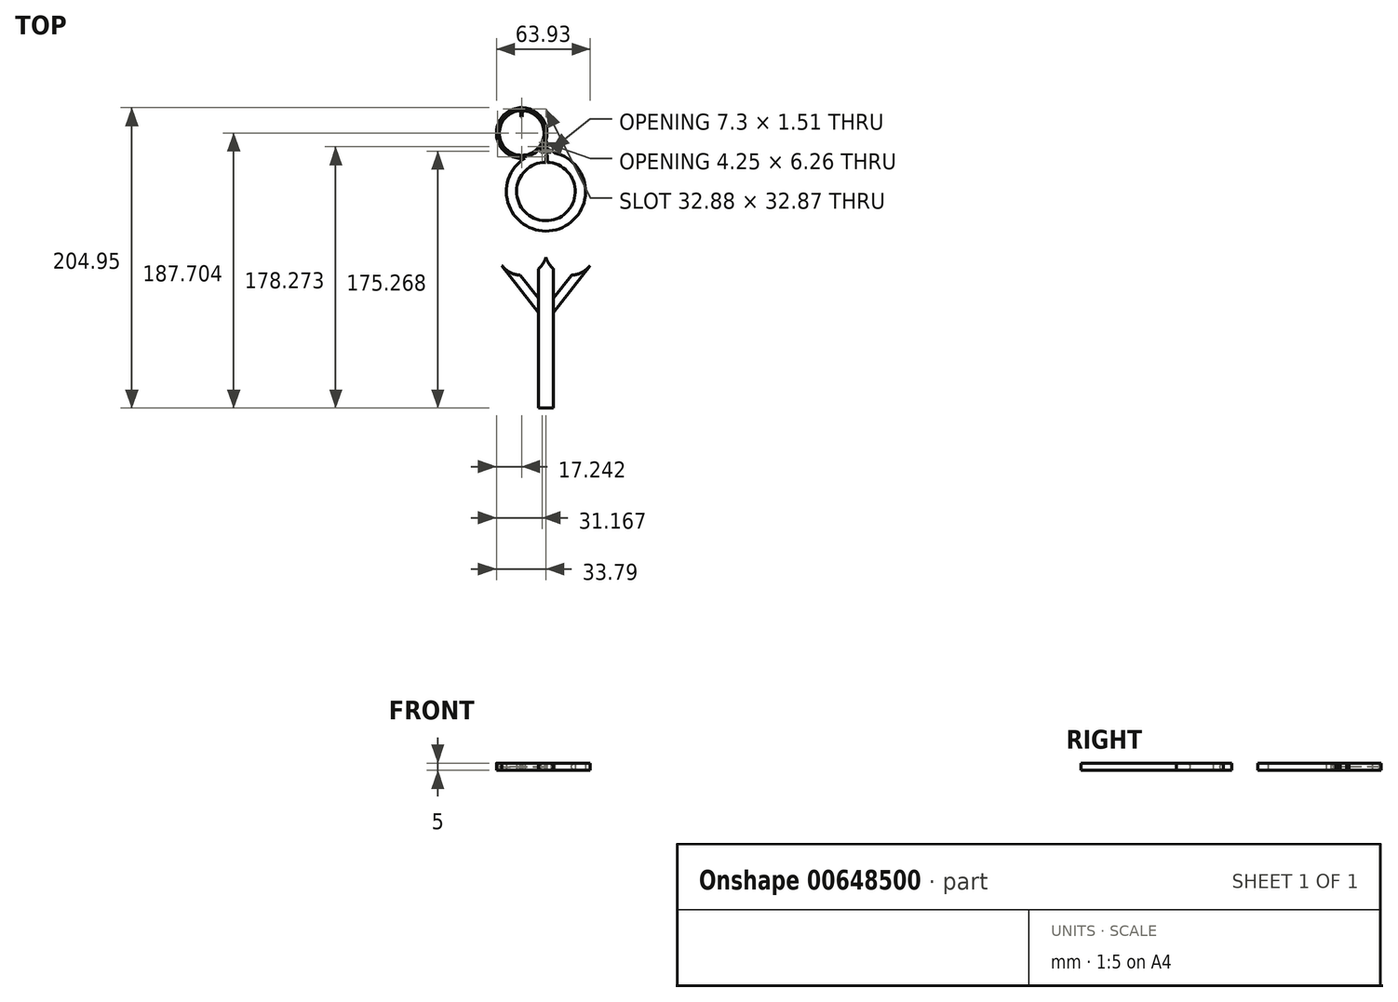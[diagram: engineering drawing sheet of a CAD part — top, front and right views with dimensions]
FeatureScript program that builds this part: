
annotation { "Feature Type Name" : "Feature", "Feature Type Description" : "" }
export const myFeature = defineFeature(function(context is Context, id is Id, definition is map)
    precondition{}
    {
        {
            var Q0;
            Q0=qCreatedBy(makeId("Top.planeOp"),FACE);
            var sketch = newSketch(context, id + "F0", { "sketchPlane" : qUnion([Q0])});
            skCircle(sketch, "E0", {"center": v(0, 0) * mm, "radius": 20 * mm});
            skCircle(sketch, "E1", {"center": v(0, 0) * mm, "radius": 27 * mm});
            skSolve(sketch);
        }
        {
            var Q0;
            Q0=qCreatedBy(makeId("Top.planeOp"),FACE);
            var sketch = newSketch(context, id + "F1", { "sketchPlane" : qUnion([Q0])});
            skLineSegment(sketch, "E2", {"start": v(0, 60) * mm, "end": v(0, -60) * mm, "construction": true});
            skLineSegment(sketch, "E3", {"start": v(-42.43, 42.43) * mm, "end": v(42.43, -42.43) * mm, "construction": true});
            skCircle(sketch, "E4.MirrorC", {"center": v(-16.55, 39.95) * mm, "radius": 17.24 * mm});
            skCircle(sketch, "E5", {"center": v(0, 0) * mm, "radius": 26 * mm, "construction": true});
            skLineSegment(sketch, "E6", {"start": v(1.05, 60) * mm, "end": v(0, 0) * mm, "construction": true});
            skLineSegment(sketch, "E7", {"start": v(0, 0) * mm, "end": v(-43.16, 41.68) * mm, "construction": true});
            skCircle(sketch, "E8", {"center": v(-16.55, 39.95) * mm, "radius": 15.24 * mm});
            skSolve(sketch);
        }
        {
            var Q0;
            Q0=makeQuery(id+"F0.imprint","IMPRINT",FACE,{"disambiguationData":[TD([[makeQuery(id+"F0.imprint","IMPRINT",EDGE,{"derivedFrom":sQuery(id+"F0.wireOp",EDGE,"E0")}),-1.0]])]});
            extrude(context, id + "F2", {"entities" : qUnion([Q0]), "depth" : 5 * mm, "offsetDistance" : 25 * mm});
        }
        {
            var Q0;
            Q0=makeQuery(id+"F2.opExtrude","CAP_FACE",FACE,{"disambiguationData":[OSD([sQuery(id+"F0.wireOp",EDGE,"E0"),sQuery(id+"F0.wireOp",EDGE,"E1")])],"isStart":false});
            var sketch = newSketch(context, id + "F3", { "sketchPlane" : qUnion([Q0])});
            skLineSegment(sketch, "E9", {"start": v(0, 20) * mm, "end": v(0, 25) * mm});
            skArc(sketch, "E10", {"start": v(1.1, 24.98) * mm, "mid": v(0.55, 25) * mm, "end": v(0, 25) * mm});
            skLineSegment(sketch, "E11", {"start": v(0.87, 19.98) * mm, "end": v(1.1, 24.98) * mm});
            skArc(sketch, "E12", {"start": v(0.87, 19.98) * mm, "mid": v(0.44, 20) * mm, "end": v(0, 20) * mm});
            skSolve(sketch);
        }
        {
            var Q0;
            Q0=qCreatedBy(makeId("Right.planeOp"),FACE);
            var sketch = newSketch(context, id + "F4", { "sketchPlane" : qUnion([Q0])});
            skLineSegment(sketch, "E13", {"start": v(0, 0) * mm, "end": v(0, 40) * mm, "construction": true});
            skSolve(sketch);
        }
        {
            var Q0;
            Q0=makeQuery(id+"F3.imprint","IMPRINT",FACE,{"disambiguationData":[TD([[makeQuery(id+"F3.imprint","IMPRINT",EDGE,{"derivedFrom":sQuery(id+"F3.wireOp",EDGE,"E9")}),-1.0]])]});
            extrude(context, id + "F5", {"entities" : qUnion([Q0]), "operationType" : NewBodyOperationType.REMOVE, "oppositeDirection" : true, "depth" : 6 * mm, "offsetDistance" : 25 * mm});
        }
        {
            var Q0;
            Q0=makeQuery(id+"F5.boolean.opBoolean","INTERSECT",EDGE,{"derivedFrom":[makeQuery(id+"F2.opExtrude","CAP_FACE",FACE,{"disambiguationData":[OSD([sQuery(id+"F0.wireOp",EDGE,"E0"),sQuery(id+"F0.wireOp",EDGE,"E1")])],"isStart":true}),makeQuery(id+"F5.opExtrude","SWEPT_FACE",FACE,{"disambiguationData":[OSD([sQuery(id+"F3.wireOp",EDGE,"E10")])]})]});
            var Q1;
            Q1=makeQuery(id+"F5.boolean.opBoolean","COPY",EDGE,{"derivedFrom":makeQuery(id+"F5.opExtrude","CAP_EDGE",EDGE,{"disambiguationData":[OSD([sQuery(id+"F3.wireOp",EDGE,"E10")])],"isStart":true})});
            chamfer(context, id + "F6", {"entities" : qUnion([Q0, Q1]), "width" : 1.5 * mm, "tangentPropagation" : true});
        }
        {
            var Q0;
            Q0=makeQuery(id+"F1.imprint","IMPRINT",FACE,{"disambiguationData":[TD([[makeQuery(id+"F1.imprint","IMPRINT",EDGE,{"derivedFrom":sQuery(id+"F1.wireOp",EDGE,"E4.MirrorC")}),1.0]])]});
            extrude(context, id + "F7", {"entities" : qUnion([Q0]), "operationType" : NewBodyOperationType.ADD, "depth" : 5 * mm, "offsetDistance" : 25 * mm});
        }
        {
            var Q0;
            Q0=makeQuery(id+"F7.opExtrude","CAP_EDGE",EDGE,{"disambiguationData":[OSD([sQuery(id+"F1.wireOp",EDGE,"E8")])],"isStart":false});
            var Q1;
            Q1=makeQuery(id+"F7.opExtrude","CAP_EDGE",EDGE,{"disambiguationData":[OSD([sQuery(id+"F1.wireOp",EDGE,"E8")])],"isStart":true});
            chamfer(context, id + "F8", {"entities" : qUnion([Q0, Q1]), "chamferType" : ChamferType.TWO_OFFSETS, "width1" : 2.5 * mm, "oppositeDirection" : false, "width2" : 1.2 * mm, "tangentPropagation" : true});
        }
        {
            var Q0;
            Q0=qCreatedBy(makeId("Top.planeOp"),FACE);
            var sketch = newSketch(context, id + "F9", { "sketchPlane" : qUnion([Q0])});
            skLineSegment(sketch, "E14", {"start": v(-17, 50.94) * mm, "end": v(-17.24, 56.38) * mm});
            skLineSegment(sketch, "E15", {"start": v(-16.09, 50.94) * mm, "end": v(-15.86, 56.38) * mm});
            skLineSegment(sketch, "E16", {"start": v(-16.55, 39.95) * mm, "end": v(-16.55, 61.95) * mm, "construction": true});
            skArc(sketch, "E17", {"start": v(-16.09, 50.94) * mm, "mid": v(-16.55, 50.95) * mm, "end": v(-17, 50.94) * mm});
            skArc(sketch, "E18", {"start": v(-15.86, 56.38) * mm, "mid": v(-16.55, 56.4) * mm, "end": v(-17.24, 56.38) * mm});
            skSolve(sketch);
        }
        {
            var Q0;
            Q0=makeQuery(id+"F9.imprint","IMPRINT",FACE,{"disambiguationData":[TD([[makeQuery(id+"F9.imprint","IMPRINT",EDGE,{"derivedFrom":sQuery(id+"F9.wireOp",EDGE,"E14")}),-1.0]])]});
            extrude(context, id + "F10", {"entities" : qUnion([Q0]), "operationType" : NewBodyOperationType.ADD, "depth" : 5 * mm, "offsetDistance" : 25 * mm});
        }
        {
            var Q0;
            Q0=qCreatedBy(makeId("Right.planeOp"),FACE);
            var Q1;
            Q1=sQuery(id+"F1.wireOp",VERTEX,"E4.MirrorC.center");
            cPlane(context, id + "F11", {"entities" : qUnion([Q0, Q1]), "cplaneType" : CPlaneType.PLANE_POINT, "offset" : 25 * mm, "width" : 150 * mm, "height" : 150 * mm});
        }
        {
            var Q0;
            Q0=qCreatedBy(id+"F11.planeOp",FACE);
            var sketch = newSketch(context, id + "F12", { "sketchPlane" : qUnion([Q0])});
            skLineSegment(sketch, "E19", {"start": v(39.95, 0) * mm, "end": v(39.95, 30) * mm, "construction": true});
            skSolve(sketch);
        }
        {
            var Q0;
            Q0=qCreatedBy(makeId("Front.planeOp"),FACE);
            var sketch = newSketch(context, id + "F13", { "sketchPlane" : qUnion([Q0])});
            skLineSegment(sketch, "E20", {"start": v(0, 0) * mm, "end": v(0, 15) * mm, "construction": true});
            skSolve(sketch);
        }
        {
            var Q0;
            Q0=qCreatedBy(makeId("Top.planeOp"),FACE);
            var sketch = newSketch(context, id + "F14", { "sketchPlane" : qUnion([Q0])});
            skArc(sketch, "E21.0", {"start": v(-31.68, -31.68) * mm, "mid": v(-23.15, -55.88) * mm, "end": v(0, -44.8) * mm});
            skArc(sketch, "E22.0", {"start": v(0, -44.8) * mm, "mid": v(23.15, -55.88) * mm, "end": v(31.68, -31.68) * mm});
            skLineSegment(sketch, "E23", {"start": v(-5, -147.76) * mm, "end": v(-5, -52.76) * mm});
            skLineSegment(sketch, "E24.MirrorCS", {"start": v(5, -147.76) * mm, "end": v(5, -52.76) * mm});
            skLineSegment(sketch, "E25", {"start": v(-5, -147.76) * mm, "end": v(5, -147.76) * mm});
            skSolve(sketch);
        }
        {
            var Q0;
            Q0=qCreatedBy(makeId("Top.planeOp"),FACE);
            var sketch = newSketch(context, id + "F15", { "sketchPlane" : qUnion([Q0])});
            skArc(sketch, "E26.0", {"start": v(-30.14, -50.57) * mm, "mid": v(-24.47, -55.27) * mm, "end": v(-17.36, -57.18) * mm});
            skLineSegment(sketch, "E27", {"start": v(-5, -82.74) * mm, "end": v(-30.14, -50.57) * mm});
            skLineSegment(sketch, "E28", {"start": v(-17.36, -57.18) * mm, "end": v(-5, -73) * mm});
            skLineSegment(sketch, "E29", {"start": v(-5, -73) * mm, "end": v(-5, -82.74) * mm});
            skPoint(sketch, "E30.orphan", {"position": v(0, -44.8) * mm});
            skPoint(sketch, "E31.orphan", {"position": v(-31.68, -31.68) * mm});
            skPoint(sketch, "E32.0.end.orphan", {"position": v(31.68, -31.68) * mm});
            skLineSegment(sketch, "E33.MirrorCS", {"start": v(17.36, -57.18) * mm, "end": v(5, -73) * mm});
            skArc(sketch, "E34.MirrorCS", {"start": v(30.14, -50.57) * mm, "mid": v(24.47, -55.27) * mm, "end": v(17.36, -57.18) * mm});
            skLineSegment(sketch, "E35.MirrorCS", {"start": v(5, -82.74) * mm, "end": v(30.14, -50.57) * mm});
            skLineSegment(sketch, "E36.MirrorCS", {"start": v(5, -73) * mm, "end": v(5, -82.74) * mm});
            skSolve(sketch);
        }
        {
            var Q0;
            {var subQ1=sQuery(id+"F14.wireOp",EDGE,"E23");Q0=makeQuery(id+"F14.imprint","IMPRINT",FACE,{"disambiguationData":[TD([[makeQuery(id+"F14.imprint","IMPRINT",EDGE,{"derivedFrom":subQ1}),-1.0]])]});}
            var Q1;
            Q1=makeQuery(id+"F15.imprint","IMPRINT",FACE,{"disambiguationData":[TD([[makeQuery(id+"F15.imprint","IMPRINT",EDGE,{"derivedFrom":sQuery(id+"F15.wireOp",EDGE,"E26.0")}),-1.0]])]});
            var Q2;
            Q2=makeQuery(id+"F15.imprint","IMPRINT",FACE,{"disambiguationData":[TD([[makeQuery(id+"F15.imprint","IMPRINT",EDGE,{"derivedFrom":sQuery(id+"F15.wireOp",EDGE,"E33.MirrorCS")}),1.0]])]});
            extrude(context, id + "F16", {"entities" : qUnion([Q0, Q1, Q2]), "operationType" : NewBodyOperationType.ADD, "depth" : 5 * mm, "offsetDistance" : 25 * mm});
        }
        {
            var Q0;
            {var subQ1=sQuery(id+"F1.wireOp",EDGE,"E4.MirrorC");var subQ6=sQuery(id+"F14.wireOp",EDGE,"E24.MirrorCS");Q0=makeQuery(id+"F16.boolean.opBoolean","SPLIT",EDGE,{"disambiguationData":[TD([makeQuery(id+"Ff9FOJwP5qnnYWK_1.4.F7.opExtrude","SWEPT_FACE",FACE,{"disambiguationData":[OSD([subQ1])]})])],"derivedFrom":makeQuery(id+"F16.opExtrude","CAP_EDGE",EDGE,{"disambiguationData":[OSD([subQ6])],"isStart":false})});}
            var Q1;
            {var subQ1=sQuery(id+"F1.wireOp",EDGE,"E4.MirrorC");var subQ6=sQuery(id+"F14.wireOp",EDGE,"E23");Q1=makeQuery(id+"F16.boolean.opBoolean","SPLIT",EDGE,{"disambiguationData":[TD([makeQuery(id+"Ff9FOJwP5qnnYWK_1.3.F7.opExtrude","SWEPT_FACE",FACE,{"disambiguationData":[OSD([subQ1])]})])],"derivedFrom":makeQuery(id+"F16.opExtrude","CAP_EDGE",EDGE,{"disambiguationData":[OSD([subQ6])],"isStart":false})});}
            var Q2;
            {var subQ1=sQuery(id+"F1.wireOp",EDGE,"E4.MirrorC");var subQ6=sQuery(id+"F14.wireOp",EDGE,"E23");Q2=makeQuery(id+"F16.boolean.opBoolean","SPLIT",EDGE,{"disambiguationData":[TD([makeQuery(id+"Ff9FOJwP5qnnYWK_1.3.F7.opExtrude","SWEPT_FACE",FACE,{"disambiguationData":[OSD([subQ1])]})])],"derivedFrom":makeQuery(id+"F16.opExtrude","CAP_EDGE",EDGE,{"disambiguationData":[OSD([subQ6])],"isStart":true})});}
            var Q3;
            {var subQ1=sQuery(id+"F1.wireOp",EDGE,"E4.MirrorC");var subQ6=sQuery(id+"F14.wireOp",EDGE,"E24.MirrorCS");Q3=makeQuery(id+"F16.boolean.opBoolean","SPLIT",EDGE,{"disambiguationData":[TD([makeQuery(id+"Ff9FOJwP5qnnYWK_1.4.F7.opExtrude","SWEPT_FACE",FACE,{"disambiguationData":[OSD([subQ1])]})])],"derivedFrom":makeQuery(id+"F16.opExtrude","CAP_EDGE",EDGE,{"disambiguationData":[OSD([subQ6])],"isStart":true})});}
            var Q4;
            {var subQ6=sQuery(id+"F14.wireOp",EDGE,"E25");var subQ7=sQuery(id+"F14.wireOp",EDGE,"E23");Q4=makeQuery(id+"F16.boolean.opBoolean","SPLIT",EDGE,{"disambiguationData":[TD([makeQuery(id+"F16.opExtrude","SWEPT_FACE",FACE,{"disambiguationData":[OSD([subQ6])]})])],"derivedFrom":makeQuery(id+"F16.opExtrude","CAP_EDGE",EDGE,{"disambiguationData":[OSD([subQ7])],"isStart":true})});}
            var Q5;
            {var subQ6=sQuery(id+"F14.wireOp",EDGE,"E25");var subQ7=sQuery(id+"F14.wireOp",EDGE,"E24.MirrorCS");Q5=makeQuery(id+"F16.boolean.opBoolean","SPLIT",EDGE,{"disambiguationData":[TD([makeQuery(id+"F16.opExtrude","SWEPT_FACE",FACE,{"disambiguationData":[OSD([subQ6])]})])],"derivedFrom":makeQuery(id+"F16.opExtrude","CAP_EDGE",EDGE,{"disambiguationData":[OSD([subQ7])],"isStart":true})});}
            var Q6;
            {var subQ7=sQuery(id+"F14.wireOp",EDGE,"E25");var subQ8=sQuery(id+"F14.wireOp",EDGE,"E24.MirrorCS");Q6=makeQuery(id+"F16.boolean.opBoolean","SPLIT",EDGE,{"disambiguationData":[TD([makeQuery(id+"F16.opExtrude","SWEPT_FACE",FACE,{"disambiguationData":[OSD([subQ7])]})])],"derivedFrom":makeQuery(id+"F16.opExtrude","CAP_EDGE",EDGE,{"disambiguationData":[OSD([subQ8])],"isStart":false})});}
            var Q7;
            {var subQ6=sQuery(id+"F14.wireOp",EDGE,"E25");var subQ7=sQuery(id+"F14.wireOp",EDGE,"E23");Q7=makeQuery(id+"F16.boolean.opBoolean","SPLIT",EDGE,{"disambiguationData":[TD([makeQuery(id+"F16.opExtrude","SWEPT_FACE",FACE,{"disambiguationData":[OSD([subQ6])]})])],"derivedFrom":makeQuery(id+"F16.opExtrude","CAP_EDGE",EDGE,{"disambiguationData":[OSD([subQ7])],"isStart":false})});}
            fillet(context, id + "F17", {"entities" : qUnion([Q0, Q1, Q2, Q3, Q4, Q5, Q6, Q7]), "radius" : 2.5 * mm, "tangentPropagation" : true, "allowEdgeOverflow" : false});
        }
        {
            var Q0;
            Q0=makeQuery(id+"F16.opExtrude","CAP_EDGE",EDGE,{"disambiguationData":[OSD([sQuery(id+"F15.wireOp",EDGE,"E28")])],"isStart":false});
            var Q1;
            Q1=makeQuery(id+"F16.opExtrude","CAP_EDGE",EDGE,{"disambiguationData":[OSD([sQuery(id+"F15.wireOp",EDGE,"E28")])],"isStart":true});
            var Q2;
            Q2=makeQuery(id+"F16.opExtrude","CAP_EDGE",EDGE,{"disambiguationData":[OSD([sQuery(id+"F15.wireOp",EDGE,"E33.MirrorCS")])],"isStart":true});
            var Q3;
            Q3=makeQuery(id+"F16.opExtrude","CAP_EDGE",EDGE,{"disambiguationData":[OSD([sQuery(id+"F15.wireOp",EDGE,"E33.MirrorCS")])],"isStart":false});
            fillet(context, id + "F18", {"entities" : qUnion([Q0, Q1, Q2, Q3]), "radius" : 2.5 * mm, "tangentPropagation" : true, "allowEdgeOverflow" : false});
        }
        {
            var Q0;
            Q0=qCreatedBy(makeId("Top.planeOp"),FACE);
            var sketch = newSketch(context, id + "F19", { "sketchPlane" : qUnion([Q0])});
            skArc(sketch, "E37.0", {"start": v(-0.5, 33.64) * mm, "mid": v(-0.23, 34.37) * mm, "end": v(0, 35.1) * mm});
            skArc(sketch, "E38.0", {"start": v(0, 35.1) * mm, "mid": v(0.23, 34.37) * mm, "end": v(0.5, 33.64) * mm});
            skArc(sketch, "E39.0", {"start": v(5.97, 26.33) * mm, "mid": v(4.82, 26.57) * mm, "end": v(3.65, 26.75) * mm});
            skLineSegment(sketch, "E40", {"start": v(-0.5, 33.64) * mm, "end": v(-0.5, 29.14) * mm});
            skLineSegment(sketch, "E41.MirrorCS", {"start": v(0.5, 33.64) * mm, "end": v(0.5, 29.14) * mm});
            skLineSegment(sketch, "E42", {"start": v(-4.66, 26.87) * mm, "end": v(-5.97, 26.33) * mm, "construction": true});
            skLineSegment(sketch, "E43", {"start": v(-0.5, 29.14) * mm, "end": v(-4.75, 27.38) * mm});
            skLineSegment(sketch, "E44.MirrorCS", {"start": v(0, 28.26) * mm, "end": v(-3.65, 26.75) * mm});
            skPoint(sketch, "E45.orphan", {"position": v(-3.65, 26.75) * mm});
            skLineSegment(sketch, "E46.MirrorCS", {"start": v(0.5, 29.14) * mm, "end": v(4.75, 27.38) * mm});
            skLineSegment(sketch, "E47.MirrorCS", {"start": v(0, 28.26) * mm, "end": v(3.65, 26.75) * mm});
            skArc(sketch, "E48.trimOffspring", {"start": v(-3.65, 26.75) * mm, "mid": v(-4.82, 26.57) * mm, "end": v(-5.97, 26.33) * mm});
            skArc(sketch, "E49.trimOffspring", {"start": v(-5.97, 26.33) * mm, "mid": v(-5.35, 26.84) * mm, "end": v(-4.75, 27.38) * mm});
            skArc(sketch, "E50.MirrorCS", {"start": v(5.97, 26.33) * mm, "mid": v(5.35, 26.84) * mm, "end": v(4.75, 27.38) * mm});
            skPoint(sketch, "E51.orphan", {"position": v(-0.16, 29.28) * mm});
            skPoint(sketch, "E52.orphan", {"position": v(0.16, 29.28) * mm});
            skPoint(sketch, "E53.orphan", {"position": v(-0.5, 28.64) * mm});
            skPoint(sketch, "E54.orphan", {"position": v(-0.22, 28.36) * mm});
            skPoint(sketch, "E55.orphan", {"position": v(0.22, 28.36) * mm});
            skPoint(sketch, "E56.orphan", {"position": v(0.5, 28.64) * mm});
            skPoint(sketch, "E57.end.orphan", {"position": v(0, 28.64) * mm});
            skSolve(sketch);
        }
        {
            var Q0;
            Q0=makeQuery(id+"F19.imprint","IMPRINT",FACE,{"disambiguationData":[TD([[makeQuery(id+"F19.imprint","IMPRINT",EDGE,{"derivedFrom":sQuery(id+"F19.wireOp",EDGE,"E37.0")}),-1.0]])]});
            extrude(context, id + "F20", {"entities" : qUnion([Q0]), "operationType" : NewBodyOperationType.ADD, "depth" : 5 * mm, "offsetDistance" : 25 * mm});
        }
    });
